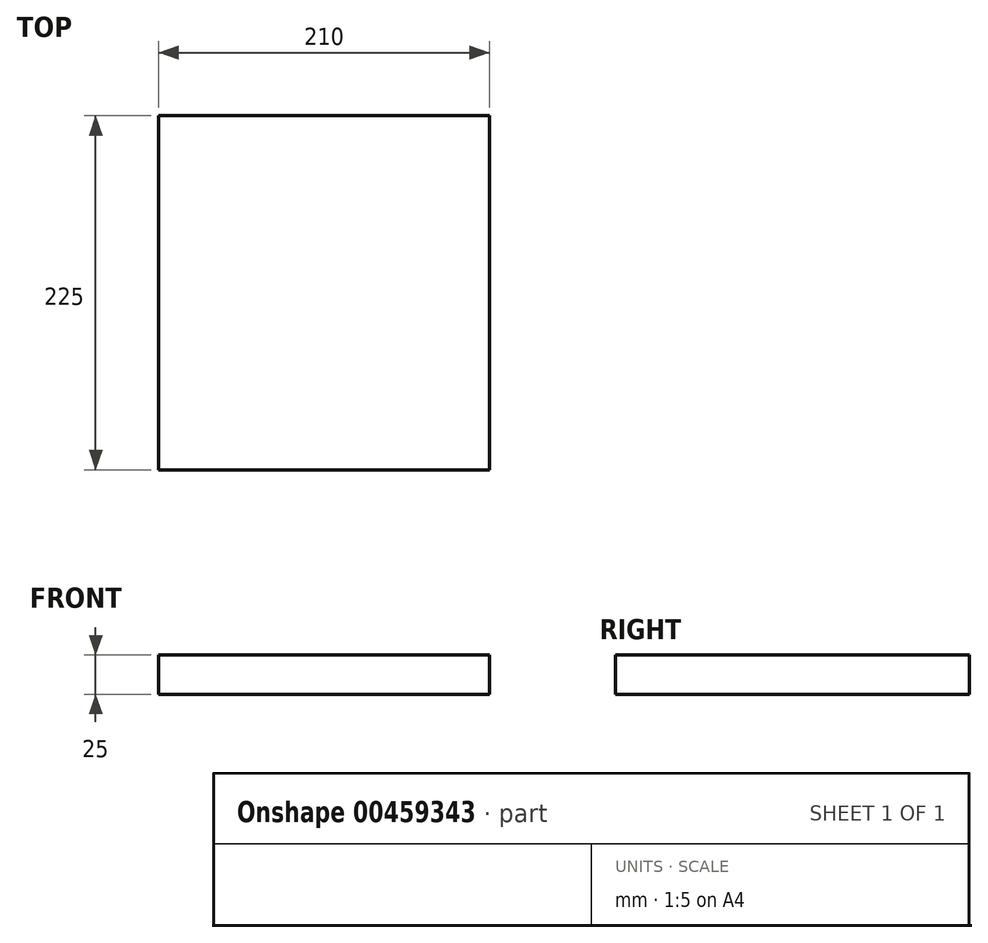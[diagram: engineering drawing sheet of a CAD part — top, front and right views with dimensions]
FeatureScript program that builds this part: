
annotation { "Feature Type Name" : "Feature", "Feature Type Description" : "" }
export const myFeature = defineFeature(function(context is Context, id is Id, definition is map)
    precondition{}
    {
        {
            var Q0;
            Q0=qCreatedBy(makeId("Top.planeOp"),FACE);
            var sketch = newSketch(context, id + "F0", { "sketchPlane" : qUnion([Q0])});
            skLineSegment(sketch, "E0.bottom", {"start": v(-70.15, 140.95) * mm, "end": v(139.85, 140.95) * mm});
            skLineSegment(sketch, "E0.top", {"start": v(-70.15, -84.05) * mm, "end": v(139.85, -84.05) * mm});
            skLineSegment(sketch, "E0.left", {"start": v(-70.15, 140.95) * mm, "end": v(-70.15, -84.05) * mm});
            skLineSegment(sketch, "E0.right", {"start": v(139.85, 140.95) * mm, "end": v(139.85, -84.05) * mm});
            skSolve(sketch);
        }
        {
            var Q0;
            Q0 = qSketchRegion(id + "F0", true);
            extrude(context, id + "F1", {"entities" : qUnion([Q0]), "depth" : 25 * mm});
        }
    });
